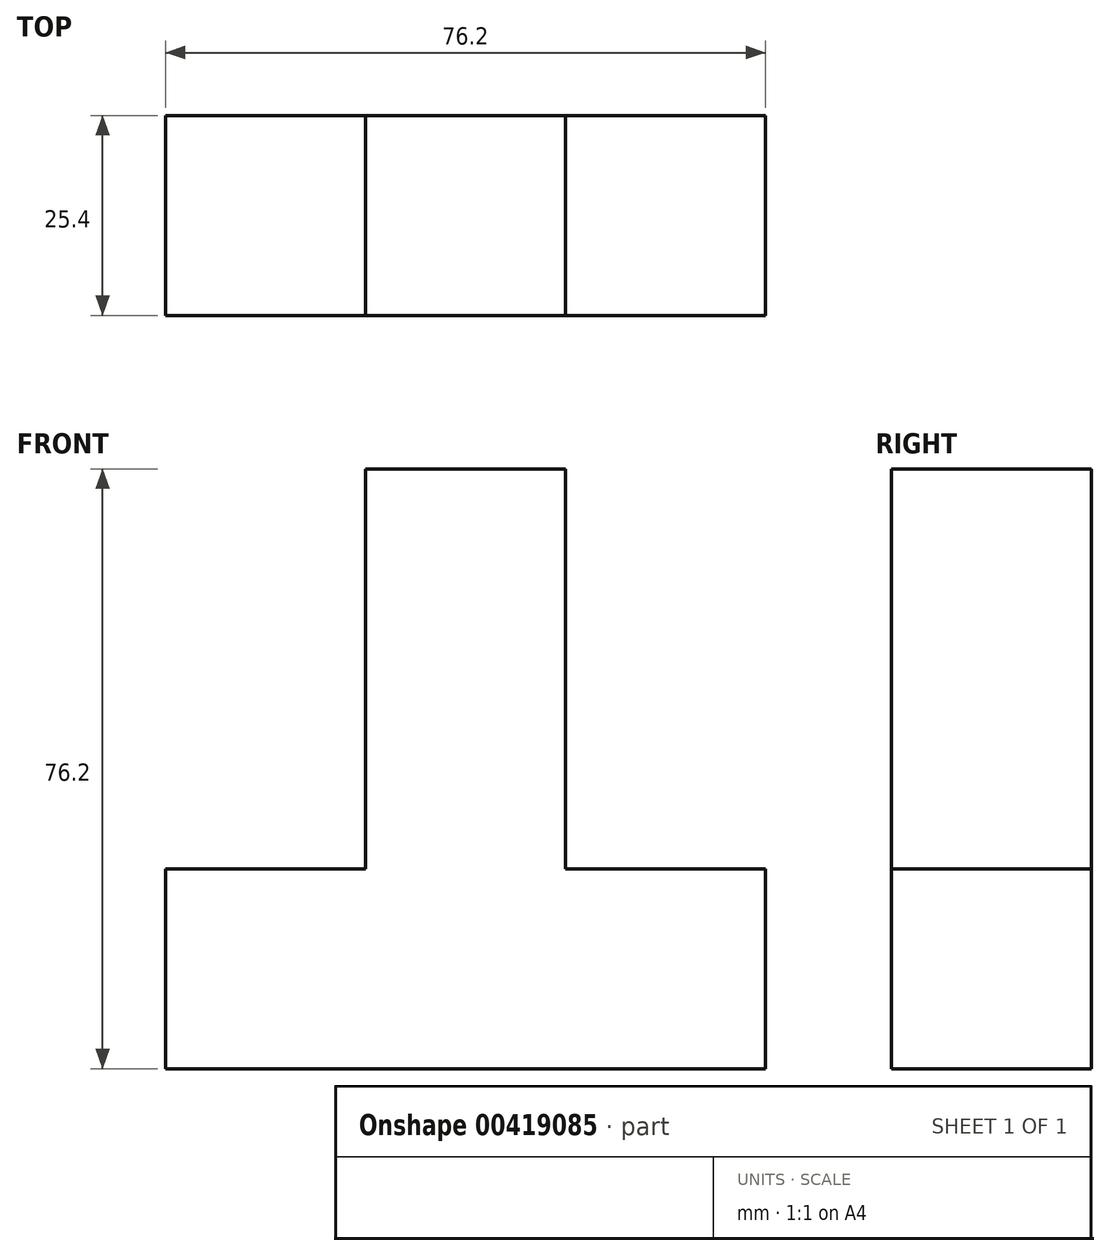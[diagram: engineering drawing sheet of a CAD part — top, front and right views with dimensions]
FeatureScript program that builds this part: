
annotation { "Feature Type Name" : "Feature", "Feature Type Description" : "" }
export const myFeature = defineFeature(function(context is Context, id is Id, definition is map)
    precondition{}
    {
        {
            var Q0;
            Q0=qCreatedBy(makeId("Front.planeOp"),FACE);
            var sketch = newSketch(context, id + "F0", { "sketchPlane" : qUnion([Q0])});
            skLineSegment(sketch, "E0", {"start": v(0, 0) * mm, "end": v(-76.2, 0) * mm});
            skLineSegment(sketch, "E1", {"start": v(-76.2, 0) * mm, "end": v(-76.2, 25.4) * mm});
            skLineSegment(sketch, "E2", {"start": v(-76.2, 25.4) * mm, "end": v(-50.8, 25.4) * mm});
            skLineSegment(sketch, "E3", {"start": v(-50.8, 25.4) * mm, "end": v(-50.8, 76.2) * mm});
            skLineSegment(sketch, "E4", {"start": v(-50.8, 76.2) * mm, "end": v(-25.4, 76.2) * mm});
            skLineSegment(sketch, "E5", {"start": v(-25.4, 76.2) * mm, "end": v(-25.4, 25.4) * mm});
            skLineSegment(sketch, "E6", {"start": v(-25.4, 25.4) * mm, "end": v(0, 25.4) * mm});
            skLineSegment(sketch, "E7", {"start": v(0, 25.4) * mm, "end": v(0, 0) * mm});
            skSolve(sketch);
        }
        {
            var Q0;
            Q0=makeQuery(id+"F0.imprint","IMPRINT",FACE,{"disambiguationData":[TD([[makeQuery(id+"F0.imprint","IMPRINT",EDGE,{"derivedFrom":sQuery(id+"F0.wireOp",EDGE,"E0")}),-1.0]])]});
            extrude(context, id + "F1", {"entities" : qUnion([Q0]), "depth" : 25.4 * mm});
        }
    });
